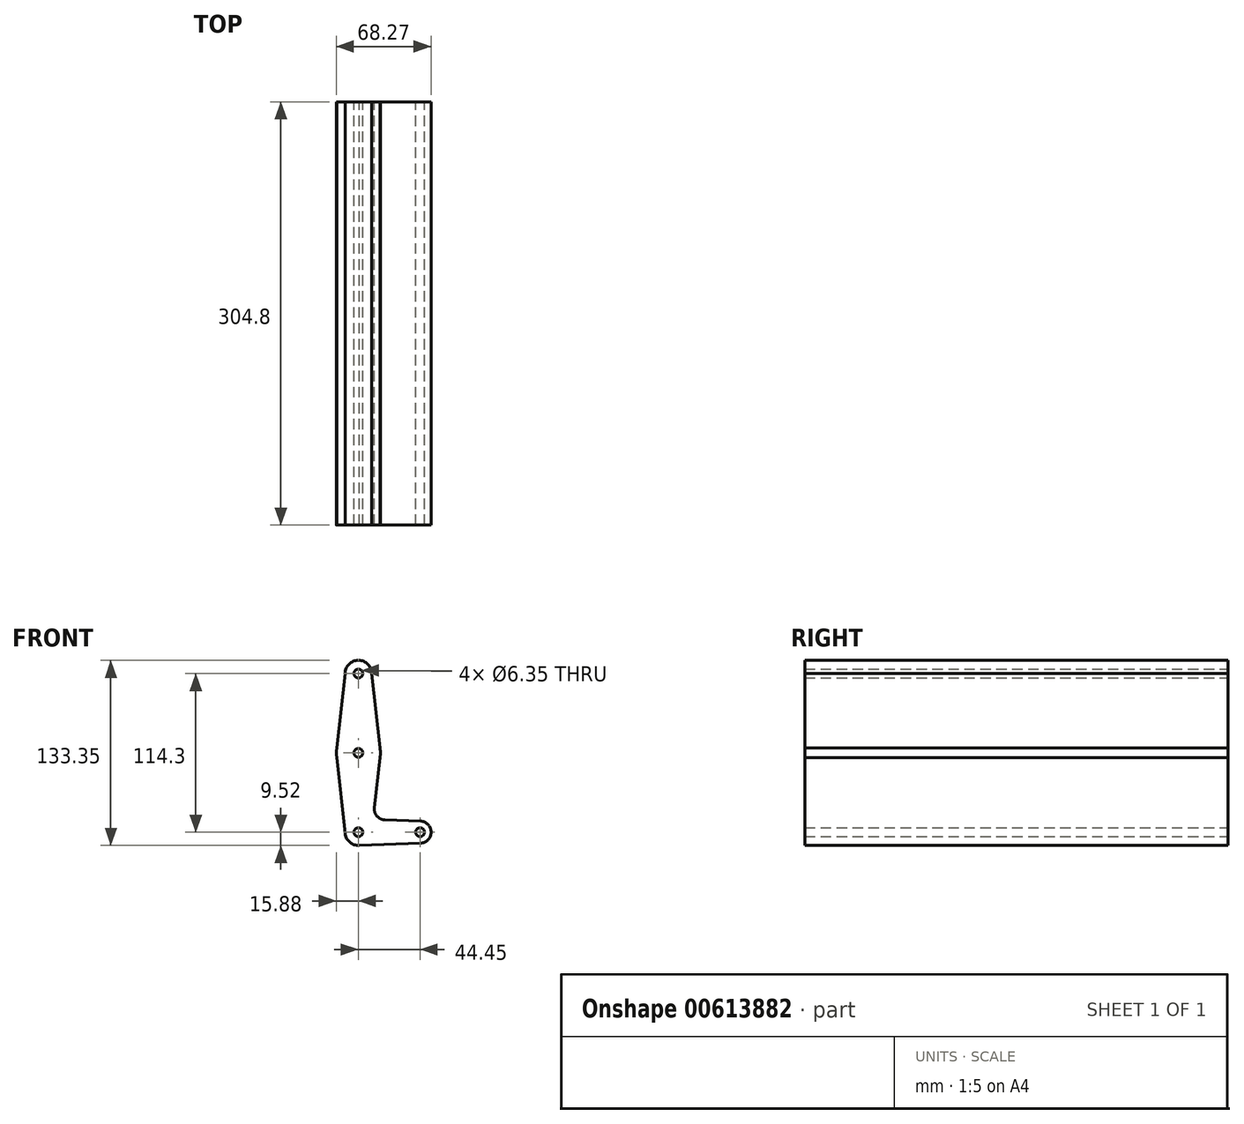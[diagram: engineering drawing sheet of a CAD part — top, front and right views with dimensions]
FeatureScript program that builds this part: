
annotation { "Feature Type Name" : "Feature", "Feature Type Description" : "" }
export const myFeature = defineFeature(function(context is Context, id is Id, definition is map)
    precondition{}
    {
        {
            var Q0;
            Q0=qCreatedBy(makeId("Front.planeOp"),FACE);
            var sketch = newSketch(context, id + "F0", { "sketchPlane" : qUnion([Q0])});
            skLineSegment(sketch, "E0", {"start": v(0, 0) * mm, "end": v(0, 57.15) * mm});
            skLineSegment(sketch, "E1", {"start": v(0, 0) * mm, "end": v(0, -57.15) * mm, "construction": true});
            skCircle(sketch, "E2", {"center": v(0, 57.15) * mm, "radius": 3.18 * mm});
            skCircle(sketch, "E3", {"center": v(0, -57.15) * mm, "radius": 3.18 * mm});
            skCircle(sketch, "E4", {"center": v(0, 57.15) * mm, "radius": 9.53 * mm});
            skCircle(sketch, "E5", {"center": v(0, -57.15) * mm, "radius": 9.53 * mm});
            skCircle(sketch, "E6", {"center": v(0, 0) * mm, "radius": 15.88 * mm});
            skCircle(sketch, "E7", {"center": v(0, 0) * mm, "radius": 3.18 * mm});
            skLineSegment(sketch, "E8", {"start": v(0, -57.15) * mm, "end": v(44.45, -57.15) * mm, "construction": true});
            skCircle(sketch, "E9", {"center": v(44.45, -57.15) * mm, "radius": 3.18 * mm});
            skCircle(sketch, "E10", {"center": v(44.45, -57.15) * mm, "radius": 7.94 * mm});
            skLineSegment(sketch, "E11", {"start": v(0, -66.68) * mm, "end": v(44.73, -65.08) * mm});
            skLineSegment(sketch, "E12", {"start": v(-15.88, 0) * mm, "end": v(-9.47, -58.2) * mm});
            skLineSegment(sketch, "E13", {"start": v(9.52, 57.15) * mm, "end": v(15.88, 0) * mm});
            skLineSegment(sketch, "E14", {"start": v(-9.52, 57.15) * mm, "end": v(-15.88, 0) * mm});
            skLineSegment(sketch, "E15", {"start": v(15.88, 0) * mm, "end": v(15.48, -3.5) * mm});
            skLineSegment(sketch, "E16", {"start": v(19.1, -48.3) * mm, "end": v(44.73, -49.22) * mm});
            skLineSegment(sketch, "E17", {"start": v(15.88, 0) * mm, "end": v(11.49, -39.48) * mm});
            skArc(sketch, "E18.filletArc", {"start": v(11.49, -39.48) * mm, "mid": v(13.37, -45.56) * mm, "end": v(19.1, -48.3) * mm});
            skSolve(sketch);
        }
        {
            var Q0;
            Q0=qSketchRegion(id+"F0",true);
            extrude(context, id + "F1", {"entities" : qUnion([Q0]), "depth" : 304.8 * mm, "offsetDistance" : 25.4 * mm});
        }
    });
